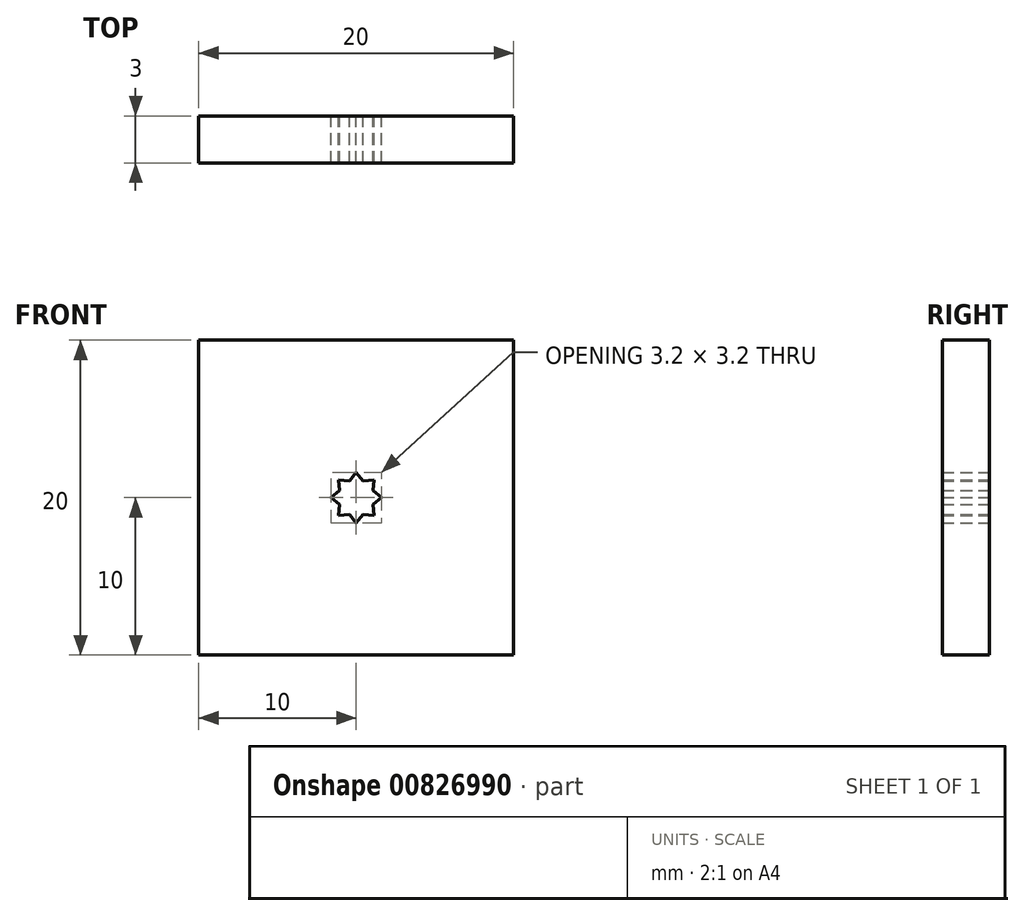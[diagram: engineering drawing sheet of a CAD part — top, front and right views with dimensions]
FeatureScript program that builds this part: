
annotation { "Feature Type Name" : "Feature", "Feature Type Description" : "" }
export const myFeature = defineFeature(function(context is Context, id is Id, definition is map)
    precondition{}
    {
        {
            var Q0;
            Q0=qCreatedBy(makeId("Front.planeOp"),FACE);
            var sketch = newSketch(context, id + "F0", { "sketchPlane" : qUnion([Q0])});
            skCircle(sketch, "E0.cCircle", {"center": v(0, 0) * mm, "radius": 1.15 * mm, "construction": true});
            skCircle(sketch, "E1.cCircle", {"center": v(0, 0) * mm, "radius": 1.6 * mm, "construction": true});
            skLineSegment(sketch, "E1.0", {"start": v(0, 1.6) * mm, "end": v(1.13, 1.13) * mm, "construction": true});
            skLineSegment(sketch, "E1.1", {"start": v(1.13, 1.13) * mm, "end": v(1.6, 0) * mm, "construction": true});
            skLineSegment(sketch, "E1.2", {"start": v(1.6, 0) * mm, "end": v(1.13, -1.13) * mm, "construction": true});
            skLineSegment(sketch, "E1.3", {"start": v(1.13, -1.13) * mm, "end": v(0, -1.6) * mm, "construction": true});
            skLineSegment(sketch, "E1.4", {"start": v(0, -1.6) * mm, "end": v(-1.13, -1.13) * mm, "construction": true});
            skLineSegment(sketch, "E1.5", {"start": v(-1.13, -1.13) * mm, "end": v(-1.6, 0) * mm, "construction": true});
            skLineSegment(sketch, "E1.6", {"start": v(-1.6, 0) * mm, "end": v(-1.13, 1.13) * mm, "construction": true});
            skLineSegment(sketch, "E1.7", {"start": v(-1.13, 1.13) * mm, "end": v(0, 1.6) * mm, "construction": true});
            skLineSegment(sketch, "E2", {"start": v(-1.13, 1.13) * mm, "end": v(-0.44, 1.06) * mm});
            skLineSegment(sketch, "E3", {"start": v(-0.44, 1.06) * mm, "end": v(0, 1.6) * mm});
            skLineSegment(sketch, "E4", {"start": v(0, 1.6) * mm, "end": v(0.44, 1.06) * mm});
            skLineSegment(sketch, "E5", {"start": v(0.44, 1.06) * mm, "end": v(1.13, 1.13) * mm});
            skLineSegment(sketch, "E6", {"start": v(1.13, 1.13) * mm, "end": v(1.06, 0.44) * mm});
            skLineSegment(sketch, "E7", {"start": v(1.06, 0.44) * mm, "end": v(1.6, 0) * mm});
            skLineSegment(sketch, "E8", {"start": v(1.6, 0) * mm, "end": v(1.06, -0.44) * mm});
            skLineSegment(sketch, "E9", {"start": v(1.06, -0.44) * mm, "end": v(1.13, -1.13) * mm});
            skLineSegment(sketch, "E10", {"start": v(1.13, -1.13) * mm, "end": v(0.44, -1.06) * mm});
            skLineSegment(sketch, "E11", {"start": v(0.44, -1.06) * mm, "end": v(0, -1.6) * mm});
            skLineSegment(sketch, "E12", {"start": v(-0.44, -1.06) * mm, "end": v(-1.13, -1.13) * mm});
            skLineSegment(sketch, "E13", {"start": v(-0.44, -1.06) * mm, "end": v(0, -1.6) * mm});
            skLineSegment(sketch, "E14", {"start": v(-1.13, -1.13) * mm, "end": v(-1.06, -0.44) * mm});
            skLineSegment(sketch, "E15", {"start": v(-1.06, -0.44) * mm, "end": v(-1.6, 0) * mm});
            skLineSegment(sketch, "E16", {"start": v(-1.6, 0) * mm, "end": v(-1.06, 0.44) * mm});
            skLineSegment(sketch, "E17", {"start": v(-1.06, 0.44) * mm, "end": v(-1.13, 1.13) * mm});
            skLineSegment(sketch, "E18.bottom", {"start": v(-10, -10) * mm, "end": v(90, -10) * mm});
            skLineSegment(sketch, "E18.top", {"start": v(-10, 70) * mm, "end": v(90, 70) * mm});
            skLineSegment(sketch, "E18.left", {"start": v(-10, -10) * mm, "end": v(-10, 70) * mm});
            skLineSegment(sketch, "E18.right", {"start": v(90, -10) * mm, "end": v(90, 70) * mm});
            skLineSegment(sketch, "E19", {"start": v(10, -10) * mm, "end": v(10, 70) * mm});
            skLineSegment(sketch, "E20", {"start": v(30, 70) * mm, "end": v(30, -10) * mm});
            skLineSegment(sketch, "E21", {"start": v(50, -10) * mm, "end": v(50, 70) * mm});
            skLineSegment(sketch, "E22", {"start": v(70, 70) * mm, "end": v(70, -10) * mm});
            skLineSegment(sketch, "E23", {"start": v(-10, 10) * mm, "end": v(90, 10) * mm});
            skLineSegment(sketch, "E24", {"start": v(-10, 30) * mm, "end": v(90, 30) * mm});
            skLineSegment(sketch, "E25", {"start": v(-10, 50) * mm, "end": v(90, 50) * mm});
            skLineSegment(sketch, "E26", {"start": v(10, -10) * mm, "end": v(30, 10) * mm, "construction": true});
            skLineSegment(sketch, "E27", {"start": v(30, -10) * mm, "end": v(50, 10) * mm, "construction": true});
            skLineSegment(sketch, "E28", {"start": v(50, 10) * mm, "end": v(70, 30) * mm, "construction": true});
            skLineSegment(sketch, "E29", {"start": v(70, 30) * mm, "end": v(90, 50) * mm, "construction": true});
            skLineSegment(sketch, "E30", {"start": v(30, 10) * mm, "end": v(50, 30) * mm, "construction": true});
            skLineSegment(sketch, "E31", {"start": v(50, 30) * mm, "end": v(70, 50) * mm, "construction": true});
            skLineSegment(sketch, "E32", {"start": v(70, 50) * mm, "end": v(90, 70) * mm, "construction": true});
            skLineSegment(sketch, "E33", {"start": v(-10, -10) * mm, "end": v(10, 10) * mm, "construction": true});
            skLineSegment(sketch, "E34", {"start": v(10, 10) * mm, "end": v(30, 30) * mm, "construction": true});
            skLineSegment(sketch, "E35", {"start": v(30, 30) * mm, "end": v(50, 50) * mm, "construction": true});
            skLineSegment(sketch, "E36", {"start": v(50, 50) * mm, "end": v(70, 70) * mm, "construction": true});
            skLineSegment(sketch, "E37", {"start": v(-10, 10) * mm, "end": v(10, 30) * mm, "construction": true});
            skLineSegment(sketch, "E38", {"start": v(10, 30) * mm, "end": v(30, 50) * mm, "construction": true});
            skLineSegment(sketch, "E39", {"start": v(30, 50) * mm, "end": v(50, 70) * mm, "construction": true});
            skLineSegment(sketch, "E40", {"start": v(-10, 30) * mm, "end": v(10, 50) * mm, "construction": true});
            skLineSegment(sketch, "E41", {"start": v(10, 50) * mm, "end": v(30, 70) * mm, "construction": true});
            skLineSegment(sketch, "E42", {"start": v(-10, 50) * mm, "end": v(10, 70) * mm, "construction": true});
            skLineSegment(sketch, "E43", {"start": v(50, -10) * mm, "end": v(70, 10) * mm, "construction": true});
            skLineSegment(sketch, "E44", {"start": v(70, 10) * mm, "end": v(90, 30) * mm, "construction": true});
            skLineSegment(sketch, "E45", {"start": v(70, -10) * mm, "end": v(90, 10) * mm, "construction": true});
            skCircle(sketch, "E46.cCircle", {"center": v(20, 0) * mm, "radius": 1.2 * mm, "construction": true});
            skCircle(sketch, "E47.cCircle", {"center": v(20, 0) * mm, "radius": 1.6 * mm, "construction": true});
            skLineSegment(sketch, "E47.0", {"start": v(20, 1.6) * mm, "end": v(21.13, 1.13) * mm, "construction": true});
            skLineSegment(sketch, "E47.1", {"start": v(21.13, 1.13) * mm, "end": v(21.6, 0) * mm, "construction": true});
            skLineSegment(sketch, "E47.2", {"start": v(21.6, 0) * mm, "end": v(21.13, -1.13) * mm, "construction": true});
            skLineSegment(sketch, "E47.3", {"start": v(21.13, -1.13) * mm, "end": v(20, -1.6) * mm, "construction": true});
            skLineSegment(sketch, "E47.4", {"start": v(20, -1.6) * mm, "end": v(18.87, -1.13) * mm, "construction": true});
            skLineSegment(sketch, "E47.5", {"start": v(18.87, -1.13) * mm, "end": v(18.4, 0) * mm, "construction": true});
            skLineSegment(sketch, "E47.6", {"start": v(18.4, 0) * mm, "end": v(18.87, 1.13) * mm, "construction": true});
            skLineSegment(sketch, "E47.7", {"start": v(18.87, 1.13) * mm, "end": v(20, 1.6) * mm, "construction": true});
            skLineSegment(sketch, "E48", {"start": v(18.87, 1.13) * mm, "end": v(19.54, 1.1) * mm});
            skLineSegment(sketch, "E49", {"start": v(19.54, 1.1) * mm, "end": v(20, 1.6) * mm});
            skLineSegment(sketch, "E50", {"start": v(20, 1.6) * mm, "end": v(20.46, 1.1) * mm});
            skLineSegment(sketch, "E51", {"start": v(20.46, 1.1) * mm, "end": v(21.13, 1.13) * mm});
            skLineSegment(sketch, "E52", {"start": v(21.13, 1.13) * mm, "end": v(21.1, 0.46) * mm});
            skLineSegment(sketch, "E53", {"start": v(21.1, 0.46) * mm, "end": v(21.6, 0) * mm});
            skLineSegment(sketch, "E54", {"start": v(21.6, 0) * mm, "end": v(21.1, -0.46) * mm});
            skLineSegment(sketch, "E55", {"start": v(21.1, -0.46) * mm, "end": v(21.13, -1.13) * mm});
            skLineSegment(sketch, "E56", {"start": v(21.13, -1.13) * mm, "end": v(20.46, -1.1) * mm});
            skLineSegment(sketch, "E57", {"start": v(20.46, -1.1) * mm, "end": v(20, -1.6) * mm});
            skLineSegment(sketch, "E58", {"start": v(19.54, -1.1) * mm, "end": v(18.87, -1.13) * mm});
            skLineSegment(sketch, "E59", {"start": v(19.54, -1.1) * mm, "end": v(20, -1.6) * mm});
            skLineSegment(sketch, "E60", {"start": v(18.87, -1.13) * mm, "end": v(18.9, -0.46) * mm});
            skLineSegment(sketch, "E61", {"start": v(18.9, -0.46) * mm, "end": v(18.4, 0) * mm});
            skLineSegment(sketch, "E62", {"start": v(18.4, 0) * mm, "end": v(18.9, 0.46) * mm});
            skLineSegment(sketch, "E63", {"start": v(18.9, 0.46) * mm, "end": v(18.87, 1.13) * mm});
            skCircle(sketch, "E64.cCircle", {"center": v(40, 0) * mm, "radius": 1.25 * mm, "construction": true});
            skCircle(sketch, "E65.cCircle", {"center": v(40, 0) * mm, "radius": 1.6 * mm, "construction": true});
            skLineSegment(sketch, "E65.0", {"start": v(40, 1.6) * mm, "end": v(41.13, 1.13) * mm, "construction": true});
            skLineSegment(sketch, "E65.1", {"start": v(41.13, 1.13) * mm, "end": v(41.6, 0) * mm, "construction": true});
            skLineSegment(sketch, "E65.2", {"start": v(41.6, 0) * mm, "end": v(41.13, -1.13) * mm, "construction": true});
            skLineSegment(sketch, "E65.3", {"start": v(41.13, -1.13) * mm, "end": v(40, -1.6) * mm, "construction": true});
            skLineSegment(sketch, "E65.4", {"start": v(40, -1.6) * mm, "end": v(38.87, -1.13) * mm, "construction": true});
            skLineSegment(sketch, "E65.5", {"start": v(38.87, -1.13) * mm, "end": v(38.4, 0) * mm, "construction": true});
            skLineSegment(sketch, "E65.6", {"start": v(38.4, 0) * mm, "end": v(38.87, 1.13) * mm, "construction": true});
            skLineSegment(sketch, "E65.7", {"start": v(38.87, 1.13) * mm, "end": v(40, 1.6) * mm, "construction": true});
            skLineSegment(sketch, "E66", {"start": v(38.87, 1.13) * mm, "end": v(39.52, 1.15) * mm});
            skLineSegment(sketch, "E67", {"start": v(39.52, 1.15) * mm, "end": v(40, 1.6) * mm});
            skLineSegment(sketch, "E68", {"start": v(40, 1.6) * mm, "end": v(40.48, 1.15) * mm});
            skLineSegment(sketch, "E69", {"start": v(40.48, 1.15) * mm, "end": v(41.13, 1.13) * mm});
            skLineSegment(sketch, "E70", {"start": v(41.13, 1.13) * mm, "end": v(41.15, 0.48) * mm});
            skLineSegment(sketch, "E71", {"start": v(41.15, 0.48) * mm, "end": v(41.6, 0) * mm});
            skLineSegment(sketch, "E72", {"start": v(41.6, 0) * mm, "end": v(41.15, -0.48) * mm});
            skLineSegment(sketch, "E73", {"start": v(41.15, -0.48) * mm, "end": v(41.13, -1.13) * mm});
            skLineSegment(sketch, "E74", {"start": v(41.13, -1.13) * mm, "end": v(40.48, -1.15) * mm});
            skLineSegment(sketch, "E75", {"start": v(40.48, -1.15) * mm, "end": v(40, -1.6) * mm});
            skLineSegment(sketch, "E76", {"start": v(39.52, -1.15) * mm, "end": v(38.87, -1.13) * mm});
            skLineSegment(sketch, "E77", {"start": v(39.52, -1.15) * mm, "end": v(40, -1.6) * mm});
            skLineSegment(sketch, "E78", {"start": v(38.87, -1.13) * mm, "end": v(38.85, -0.48) * mm});
            skLineSegment(sketch, "E79", {"start": v(38.85, -0.48) * mm, "end": v(38.4, 0) * mm});
            skLineSegment(sketch, "E80", {"start": v(38.4, 0) * mm, "end": v(38.85, 0.48) * mm});
            skLineSegment(sketch, "E81", {"start": v(38.85, 0.48) * mm, "end": v(38.87, 1.13) * mm});
            skCircle(sketch, "E82.cCircle", {"center": v(60, 0) * mm, "radius": 1.3 * mm, "construction": true});
            skCircle(sketch, "E83.cCircle", {"center": v(60, 0) * mm, "radius": 1.6 * mm, "construction": true});
            skLineSegment(sketch, "E83.0", {"start": v(60, 1.6) * mm, "end": v(61.13, 1.13) * mm, "construction": true});
            skLineSegment(sketch, "E83.1", {"start": v(61.13, 1.13) * mm, "end": v(61.6, 0) * mm, "construction": true});
            skLineSegment(sketch, "E83.2", {"start": v(61.6, 0) * mm, "end": v(61.13, -1.13) * mm, "construction": true});
            skLineSegment(sketch, "E83.3", {"start": v(61.13, -1.13) * mm, "end": v(60, -1.6) * mm, "construction": true});
            skLineSegment(sketch, "E83.4", {"start": v(60, -1.6) * mm, "end": v(58.87, -1.13) * mm, "construction": true});
            skLineSegment(sketch, "E83.5", {"start": v(58.87, -1.13) * mm, "end": v(58.4, 0) * mm, "construction": true});
            skLineSegment(sketch, "E83.6", {"start": v(58.4, 0) * mm, "end": v(58.87, 1.13) * mm, "construction": true});
            skLineSegment(sketch, "E83.7", {"start": v(58.87, 1.13) * mm, "end": v(60, 1.6) * mm, "construction": true});
            skLineSegment(sketch, "E84", {"start": v(58.87, 1.13) * mm, "end": v(59.5, 1.2) * mm});
            skLineSegment(sketch, "E85", {"start": v(59.5, 1.2) * mm, "end": v(60, 1.6) * mm});
            skLineSegment(sketch, "E86", {"start": v(60, 1.6) * mm, "end": v(60.5, 1.2) * mm});
            skLineSegment(sketch, "E87", {"start": v(60.5, 1.2) * mm, "end": v(61.13, 1.13) * mm});
            skLineSegment(sketch, "E88", {"start": v(61.13, 1.13) * mm, "end": v(61.2, 0.5) * mm});
            skLineSegment(sketch, "E89", {"start": v(61.2, 0.5) * mm, "end": v(61.6, 0) * mm});
            skLineSegment(sketch, "E90", {"start": v(61.6, 0) * mm, "end": v(61.2, -0.5) * mm});
            skLineSegment(sketch, "E91", {"start": v(61.2, -0.5) * mm, "end": v(61.13, -1.13) * mm});
            skLineSegment(sketch, "E92", {"start": v(61.13, -1.13) * mm, "end": v(60.5, -1.2) * mm});
            skLineSegment(sketch, "E93", {"start": v(60.5, -1.2) * mm, "end": v(60, -1.6) * mm});
            skLineSegment(sketch, "E94", {"start": v(59.5, -1.2) * mm, "end": v(58.87, -1.13) * mm});
            skLineSegment(sketch, "E95", {"start": v(59.5, -1.2) * mm, "end": v(60, -1.6) * mm});
            skLineSegment(sketch, "E96", {"start": v(58.87, -1.13) * mm, "end": v(58.8, -0.5) * mm});
            skLineSegment(sketch, "E97", {"start": v(58.8, -0.5) * mm, "end": v(58.4, 0) * mm});
            skLineSegment(sketch, "E98", {"start": v(58.4, 0) * mm, "end": v(58.8, 0.5) * mm});
            skLineSegment(sketch, "E99", {"start": v(58.8, 0.5) * mm, "end": v(58.87, 1.13) * mm});
            skCircle(sketch, "E100.cCircle", {"center": v(80, 0) * mm, "radius": 1.35 * mm, "construction": true});
            skCircle(sketch, "E101.cCircle", {"center": v(80, 0) * mm, "radius": 1.6 * mm, "construction": true});
            skLineSegment(sketch, "E101.0", {"start": v(80, 1.6) * mm, "end": v(81.13, 1.13) * mm, "construction": true});
            skLineSegment(sketch, "E101.1", {"start": v(81.13, 1.13) * mm, "end": v(81.6, 0) * mm, "construction": true});
            skLineSegment(sketch, "E101.2", {"start": v(81.6, 0) * mm, "end": v(81.13, -1.13) * mm, "construction": true});
            skLineSegment(sketch, "E101.3", {"start": v(81.13, -1.13) * mm, "end": v(80, -1.6) * mm, "construction": true});
            skLineSegment(sketch, "E101.4", {"start": v(80, -1.6) * mm, "end": v(78.87, -1.13) * mm, "construction": true});
            skLineSegment(sketch, "E101.5", {"start": v(78.87, -1.13) * mm, "end": v(78.4, 0) * mm, "construction": true});
            skLineSegment(sketch, "E101.6", {"start": v(78.4, 0) * mm, "end": v(78.87, 1.13) * mm, "construction": true});
            skLineSegment(sketch, "E101.7", {"start": v(78.87, 1.13) * mm, "end": v(80, 1.6) * mm, "construction": true});
            skLineSegment(sketch, "E102", {"start": v(78.87, 1.13) * mm, "end": v(79.48, 1.25) * mm});
            skLineSegment(sketch, "E103", {"start": v(79.48, 1.25) * mm, "end": v(80, 1.6) * mm});
            skLineSegment(sketch, "E104", {"start": v(80, 1.6) * mm, "end": v(80.52, 1.25) * mm});
            skLineSegment(sketch, "E105", {"start": v(80.52, 1.25) * mm, "end": v(81.13, 1.13) * mm});
            skLineSegment(sketch, "E106", {"start": v(81.13, 1.13) * mm, "end": v(81.25, 0.52) * mm});
            skLineSegment(sketch, "E107", {"start": v(81.25, 0.52) * mm, "end": v(81.6, 0) * mm});
            skLineSegment(sketch, "E108", {"start": v(81.6, 0) * mm, "end": v(81.25, -0.52) * mm});
            skLineSegment(sketch, "E109", {"start": v(81.25, -0.52) * mm, "end": v(81.13, -1.13) * mm});
            skLineSegment(sketch, "E110", {"start": v(81.13, -1.13) * mm, "end": v(80.52, -1.25) * mm});
            skLineSegment(sketch, "E111", {"start": v(80.52, -1.25) * mm, "end": v(80, -1.6) * mm});
            skLineSegment(sketch, "E112", {"start": v(79.48, -1.25) * mm, "end": v(78.87, -1.13) * mm});
            skLineSegment(sketch, "E113", {"start": v(79.48, -1.25) * mm, "end": v(80, -1.6) * mm});
            skLineSegment(sketch, "E114", {"start": v(78.87, -1.13) * mm, "end": v(78.75, -0.52) * mm});
            skLineSegment(sketch, "E115", {"start": v(78.75, -0.52) * mm, "end": v(78.4, 0) * mm});
            skLineSegment(sketch, "E116", {"start": v(78.4, 0) * mm, "end": v(78.75, 0.52) * mm});
            skLineSegment(sketch, "E117", {"start": v(78.75, 0.52) * mm, "end": v(78.87, 1.13) * mm});
            skCircle(sketch, "E118.cCircle", {"center": v(0, 20) * mm, "radius": 1.15 * mm, "construction": true});
            skCircle(sketch, "E119.cCircle", {"center": v(0, 20) * mm, "radius": 1.6 * mm, "construction": true});
            skLineSegment(sketch, "E119.0", {"start": v(0, 21.6) * mm, "end": v(1.13, 21.13) * mm, "construction": true});
            skLineSegment(sketch, "E119.1", {"start": v(1.13, 21.13) * mm, "end": v(1.6, 20) * mm, "construction": true});
            skLineSegment(sketch, "E119.2", {"start": v(1.6, 20) * mm, "end": v(1.13, 18.87) * mm, "construction": true});
            skLineSegment(sketch, "E119.3", {"start": v(1.13, 18.87) * mm, "end": v(0, 18.4) * mm, "construction": true});
            skLineSegment(sketch, "E119.4", {"start": v(0, 18.4) * mm, "end": v(-1.13, 18.87) * mm, "construction": true});
            skLineSegment(sketch, "E119.5", {"start": v(-1.13, 18.87) * mm, "end": v(-1.6, 20) * mm, "construction": true});
            skLineSegment(sketch, "E119.6", {"start": v(-1.6, 20) * mm, "end": v(-1.13, 21.13) * mm, "construction": true});
            skLineSegment(sketch, "E119.7", {"start": v(-1.13, 21.13) * mm, "end": v(0, 21.6) * mm, "construction": true});
            skLineSegment(sketch, "E120", {"start": v(-1.13, 21.13) * mm, "end": v(-0.44, 21.06) * mm});
            skLineSegment(sketch, "E121", {"start": v(-0.44, 21.06) * mm, "end": v(0, 21.6) * mm});
            skLineSegment(sketch, "E122", {"start": v(0, 21.6) * mm, "end": v(0.44, 21.06) * mm});
            skLineSegment(sketch, "E123", {"start": v(0.44, 21.06) * mm, "end": v(1.13, 21.13) * mm});
            skLineSegment(sketch, "E124", {"start": v(1.13, 21.13) * mm, "end": v(1.06, 20.44) * mm});
            skLineSegment(sketch, "E125", {"start": v(1.06, 20.44) * mm, "end": v(1.6, 20) * mm});
            skLineSegment(sketch, "E126", {"start": v(1.6, 20) * mm, "end": v(1.06, 19.56) * mm});
            skLineSegment(sketch, "E127", {"start": v(1.06, 19.56) * mm, "end": v(1.13, 18.87) * mm});
            skLineSegment(sketch, "E128", {"start": v(1.13, 18.87) * mm, "end": v(0.44, 18.94) * mm});
            skLineSegment(sketch, "E129", {"start": v(0.44, 18.94) * mm, "end": v(0, 18.4) * mm});
            skLineSegment(sketch, "E130", {"start": v(-0.44, 18.94) * mm, "end": v(-1.13, 18.87) * mm});
            skLineSegment(sketch, "E131", {"start": v(-0.44, 18.94) * mm, "end": v(0, 18.4) * mm});
            skLineSegment(sketch, "E132", {"start": v(-1.13, 18.87) * mm, "end": v(-1.06, 19.56) * mm});
            skLineSegment(sketch, "E133", {"start": v(-1.06, 19.56) * mm, "end": v(-1.6, 20) * mm});
            skLineSegment(sketch, "E134", {"start": v(-1.6, 20) * mm, "end": v(-1.06, 20.44) * mm});
            skLineSegment(sketch, "E135", {"start": v(-1.06, 20.44) * mm, "end": v(-1.13, 21.13) * mm});
            skCircle(sketch, "E136.cCircle", {"center": v(20, 20) * mm, "radius": 1.2 * mm, "construction": true});
            skCircle(sketch, "E137.cCircle", {"center": v(20, 20) * mm, "radius": 1.6 * mm, "construction": true});
            skLineSegment(sketch, "E137.0", {"start": v(20, 21.6) * mm, "end": v(21.13, 21.13) * mm, "construction": true});
            skLineSegment(sketch, "E137.1", {"start": v(21.13, 21.13) * mm, "end": v(21.6, 20) * mm, "construction": true});
            skLineSegment(sketch, "E137.2", {"start": v(21.6, 20) * mm, "end": v(21.13, 18.87) * mm, "construction": true});
            skLineSegment(sketch, "E137.3", {"start": v(21.13, 18.87) * mm, "end": v(20, 18.4) * mm, "construction": true});
            skLineSegment(sketch, "E137.4", {"start": v(20, 18.4) * mm, "end": v(18.87, 18.87) * mm, "construction": true});
            skLineSegment(sketch, "E137.5", {"start": v(18.87, 18.87) * mm, "end": v(18.4, 20) * mm, "construction": true});
            skLineSegment(sketch, "E137.6", {"start": v(18.4, 20) * mm, "end": v(18.87, 21.13) * mm, "construction": true});
            skLineSegment(sketch, "E137.7", {"start": v(18.87, 21.13) * mm, "end": v(20, 21.6) * mm, "construction": true});
            skLineSegment(sketch, "E138", {"start": v(18.87, 21.13) * mm, "end": v(19.54, 21.1) * mm});
            skLineSegment(sketch, "E139", {"start": v(19.54, 21.1) * mm, "end": v(20, 21.6) * mm});
            skLineSegment(sketch, "E140", {"start": v(20, 21.6) * mm, "end": v(20.46, 21.1) * mm});
            skLineSegment(sketch, "E141", {"start": v(20.46, 21.1) * mm, "end": v(21.13, 21.13) * mm});
            skLineSegment(sketch, "E142", {"start": v(21.13, 21.13) * mm, "end": v(21.1, 20.46) * mm});
            skLineSegment(sketch, "E143", {"start": v(21.1, 20.46) * mm, "end": v(21.6, 20) * mm});
            skLineSegment(sketch, "E144", {"start": v(21.6, 20) * mm, "end": v(21.1, 19.54) * mm});
            skLineSegment(sketch, "E145", {"start": v(21.1, 19.54) * mm, "end": v(21.13, 18.87) * mm});
            skLineSegment(sketch, "E146", {"start": v(21.13, 18.87) * mm, "end": v(20.46, 18.9) * mm});
            skLineSegment(sketch, "E147", {"start": v(20.46, 18.9) * mm, "end": v(20, 18.4) * mm});
            skLineSegment(sketch, "E148", {"start": v(19.54, 18.9) * mm, "end": v(18.87, 18.87) * mm});
            skLineSegment(sketch, "E149", {"start": v(19.54, 18.9) * mm, "end": v(20, 18.4) * mm});
            skLineSegment(sketch, "E150", {"start": v(18.87, 18.87) * mm, "end": v(18.9, 19.54) * mm});
            skLineSegment(sketch, "E151", {"start": v(18.9, 19.54) * mm, "end": v(18.4, 20) * mm});
            skLineSegment(sketch, "E152", {"start": v(18.4, 20) * mm, "end": v(18.9, 20.46) * mm});
            skLineSegment(sketch, "E153", {"start": v(18.9, 20.46) * mm, "end": v(18.87, 21.13) * mm});
            skCircle(sketch, "E154.cCircle", {"center": v(40, 20) * mm, "radius": 1.6 * mm, "construction": true});
            skCircle(sketch, "E155.cCircle", {"center": v(40, 20) * mm, "radius": 2.1 * mm, "construction": true});
            skLineSegment(sketch, "E155.0", {"start": v(40, 22.1) * mm, "end": v(41.48, 21.48) * mm, "construction": true});
            skLineSegment(sketch, "E155.1", {"start": v(41.48, 21.48) * mm, "end": v(42.1, 20) * mm, "construction": true});
            skLineSegment(sketch, "E155.2", {"start": v(42.1, 20) * mm, "end": v(41.48, 18.52) * mm, "construction": true});
            skLineSegment(sketch, "E155.3", {"start": v(41.48, 18.52) * mm, "end": v(40, 17.9) * mm, "construction": true});
            skLineSegment(sketch, "E155.4", {"start": v(40, 17.9) * mm, "end": v(38.52, 18.52) * mm, "construction": true});
            skLineSegment(sketch, "E155.5", {"start": v(38.52, 18.52) * mm, "end": v(37.9, 20) * mm, "construction": true});
            skLineSegment(sketch, "E155.6", {"start": v(37.9, 20) * mm, "end": v(38.52, 21.48) * mm, "construction": true});
            skLineSegment(sketch, "E155.7", {"start": v(38.52, 21.48) * mm, "end": v(40, 22.1) * mm, "construction": true});
            skLineSegment(sketch, "E156", {"start": v(38.52, 21.48) * mm, "end": v(39.39, 21.48) * mm});
            skLineSegment(sketch, "E157", {"start": v(39.39, 21.48) * mm, "end": v(40, 22.1) * mm});
            skLineSegment(sketch, "E158", {"start": v(40, 22.1) * mm, "end": v(40.61, 21.48) * mm});
            skLineSegment(sketch, "E159", {"start": v(40.61, 21.48) * mm, "end": v(41.48, 21.48) * mm});
            skLineSegment(sketch, "E160", {"start": v(41.48, 21.48) * mm, "end": v(41.48, 20.61) * mm});
            skLineSegment(sketch, "E161", {"start": v(41.48, 20.61) * mm, "end": v(42.1, 20) * mm});
            skLineSegment(sketch, "E162", {"start": v(42.1, 20) * mm, "end": v(41.48, 19.39) * mm});
            skLineSegment(sketch, "E163", {"start": v(41.48, 19.39) * mm, "end": v(41.48, 18.52) * mm});
            skLineSegment(sketch, "E164", {"start": v(41.48, 18.52) * mm, "end": v(40.61, 18.52) * mm});
            skLineSegment(sketch, "E165", {"start": v(40.61, 18.52) * mm, "end": v(40, 17.9) * mm});
            skLineSegment(sketch, "E166", {"start": v(39.39, 18.52) * mm, "end": v(38.52, 18.52) * mm});
            skLineSegment(sketch, "E167", {"start": v(39.39, 18.52) * mm, "end": v(40, 17.9) * mm});
            skLineSegment(sketch, "E168", {"start": v(38.52, 18.52) * mm, "end": v(38.52, 19.39) * mm});
            skLineSegment(sketch, "E169", {"start": v(38.52, 19.39) * mm, "end": v(37.9, 20) * mm});
            skLineSegment(sketch, "E170", {"start": v(37.9, 20) * mm, "end": v(38.52, 20.61) * mm});
            skLineSegment(sketch, "E171", {"start": v(38.52, 20.61) * mm, "end": v(38.52, 21.48) * mm});
            skCircle(sketch, "E172.cCircle", {"center": v(60, 20) * mm, "radius": 1.3 * mm, "construction": true});
            skCircle(sketch, "E173.cCircle", {"center": v(60, 20) * mm, "radius": 1.6 * mm, "construction": true});
            skLineSegment(sketch, "E173.0", {"start": v(60, 21.6) * mm, "end": v(61.13, 21.13) * mm, "construction": true});
            skLineSegment(sketch, "E173.1", {"start": v(61.13, 21.13) * mm, "end": v(61.6, 20) * mm, "construction": true});
            skLineSegment(sketch, "E173.2", {"start": v(61.6, 20) * mm, "end": v(61.13, 18.87) * mm, "construction": true});
            skLineSegment(sketch, "E173.3", {"start": v(61.13, 18.87) * mm, "end": v(60, 18.4) * mm, "construction": true});
            skLineSegment(sketch, "E173.4", {"start": v(60, 18.4) * mm, "end": v(58.87, 18.87) * mm, "construction": true});
            skLineSegment(sketch, "E173.5", {"start": v(58.87, 18.87) * mm, "end": v(58.4, 20) * mm, "construction": true});
            skLineSegment(sketch, "E173.6", {"start": v(58.4, 20) * mm, "end": v(58.87, 21.13) * mm, "construction": true});
            skLineSegment(sketch, "E173.7", {"start": v(58.87, 21.13) * mm, "end": v(60, 21.6) * mm, "construction": true});
            skLineSegment(sketch, "E174", {"start": v(58.87, 21.13) * mm, "end": v(59.5, 21.2) * mm});
            skLineSegment(sketch, "E175", {"start": v(59.5, 21.2) * mm, "end": v(60, 21.6) * mm});
            skLineSegment(sketch, "E176", {"start": v(60, 21.6) * mm, "end": v(60.5, 21.2) * mm});
            skLineSegment(sketch, "E177", {"start": v(60.5, 21.2) * mm, "end": v(61.13, 21.13) * mm});
            skLineSegment(sketch, "E178", {"start": v(61.13, 21.13) * mm, "end": v(61.2, 20.5) * mm});
            skLineSegment(sketch, "E179", {"start": v(61.2, 20.5) * mm, "end": v(61.6, 20) * mm});
            skLineSegment(sketch, "E180", {"start": v(61.6, 20) * mm, "end": v(61.2, 19.5) * mm});
            skLineSegment(sketch, "E181", {"start": v(61.2, 19.5) * mm, "end": v(61.13, 18.87) * mm});
            skLineSegment(sketch, "E182", {"start": v(61.13, 18.87) * mm, "end": v(60.5, 18.8) * mm});
            skLineSegment(sketch, "E183", {"start": v(60.5, 18.8) * mm, "end": v(60, 18.4) * mm});
            skLineSegment(sketch, "E184", {"start": v(59.5, 18.8) * mm, "end": v(58.87, 18.87) * mm});
            skLineSegment(sketch, "E185", {"start": v(59.5, 18.8) * mm, "end": v(60, 18.4) * mm});
            skLineSegment(sketch, "E186", {"start": v(58.87, 18.87) * mm, "end": v(58.8, 19.5) * mm});
            skLineSegment(sketch, "E187", {"start": v(58.8, 19.5) * mm, "end": v(58.4, 20) * mm});
            skLineSegment(sketch, "E188", {"start": v(58.4, 20) * mm, "end": v(58.8, 20.5) * mm});
            skLineSegment(sketch, "E189", {"start": v(58.8, 20.5) * mm, "end": v(58.87, 21.13) * mm});
            skCircle(sketch, "E190.cCircle", {"center": v(80, 20) * mm, "radius": 1.35 * mm, "construction": true});
            skCircle(sketch, "E191.cCircle", {"center": v(80, 20) * mm, "radius": 1.6 * mm, "construction": true});
            skLineSegment(sketch, "E191.0", {"start": v(80, 21.6) * mm, "end": v(81.13, 21.13) * mm, "construction": true});
            skLineSegment(sketch, "E191.1", {"start": v(81.13, 21.13) * mm, "end": v(81.6, 20) * mm, "construction": true});
            skLineSegment(sketch, "E191.2", {"start": v(81.6, 20) * mm, "end": v(81.13, 18.87) * mm, "construction": true});
            skLineSegment(sketch, "E191.3", {"start": v(81.13, 18.87) * mm, "end": v(80, 18.4) * mm, "construction": true});
            skLineSegment(sketch, "E191.4", {"start": v(80, 18.4) * mm, "end": v(78.87, 18.87) * mm, "construction": true});
            skLineSegment(sketch, "E191.5", {"start": v(78.87, 18.87) * mm, "end": v(78.4, 20) * mm, "construction": true});
            skLineSegment(sketch, "E191.6", {"start": v(78.4, 20) * mm, "end": v(78.87, 21.13) * mm, "construction": true});
            skLineSegment(sketch, "E191.7", {"start": v(78.87, 21.13) * mm, "end": v(80, 21.6) * mm, "construction": true});
            skLineSegment(sketch, "E192", {"start": v(78.87, 21.13) * mm, "end": v(79.48, 21.25) * mm});
            skLineSegment(sketch, "E193", {"start": v(79.48, 21.25) * mm, "end": v(80, 21.6) * mm});
            skLineSegment(sketch, "E194", {"start": v(80, 21.6) * mm, "end": v(80.52, 21.25) * mm});
            skLineSegment(sketch, "E195", {"start": v(80.52, 21.25) * mm, "end": v(81.13, 21.13) * mm});
            skLineSegment(sketch, "E196", {"start": v(81.13, 21.13) * mm, "end": v(81.25, 20.52) * mm});
            skLineSegment(sketch, "E197", {"start": v(81.25, 20.52) * mm, "end": v(81.6, 20) * mm});
            skLineSegment(sketch, "E198", {"start": v(81.6, 20) * mm, "end": v(81.25, 19.48) * mm});
            skLineSegment(sketch, "E199", {"start": v(81.25, 19.48) * mm, "end": v(81.13, 18.87) * mm});
            skLineSegment(sketch, "E200", {"start": v(81.13, 18.87) * mm, "end": v(80.52, 18.75) * mm});
            skLineSegment(sketch, "E201", {"start": v(80.52, 18.75) * mm, "end": v(80, 18.4) * mm});
            skLineSegment(sketch, "E202", {"start": v(79.48, 18.75) * mm, "end": v(78.87, 18.87) * mm});
            skLineSegment(sketch, "E203", {"start": v(79.48, 18.75) * mm, "end": v(80, 18.4) * mm});
            skLineSegment(sketch, "E204", {"start": v(78.87, 18.87) * mm, "end": v(78.75, 19.48) * mm});
            skLineSegment(sketch, "E205", {"start": v(78.75, 19.48) * mm, "end": v(78.4, 20) * mm});
            skLineSegment(sketch, "E206", {"start": v(78.4, 20) * mm, "end": v(78.75, 20.52) * mm});
            skLineSegment(sketch, "E207", {"start": v(78.75, 20.52) * mm, "end": v(78.87, 21.13) * mm});
            skSolve(sketch);
        }
        {
            var Q0;
            Q0=makeQuery(id+"F0.imprint","IMPRINT",FACE,{"disambiguationData":[TD([[makeQuery(id+"F0.imprint","IMPRINT",EDGE,{"derivedFrom":sQuery(id+"F0.wireOp",EDGE,"E2")}),1.0]])]});
            extrude(context, id + "F1", {"entities" : qUnion([Q0]), "depth" : 3 * mm, "offsetDistance" : 25 * mm});
        }
    });
